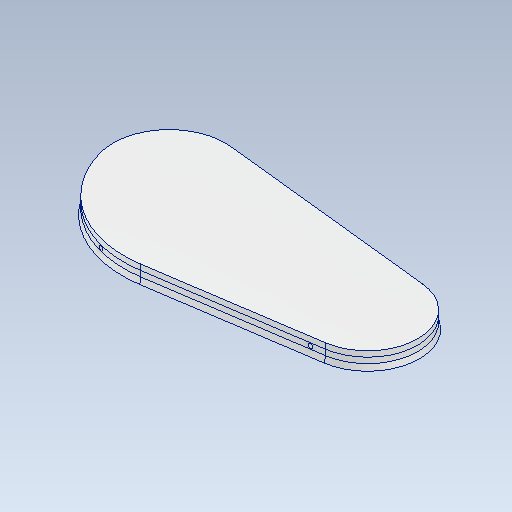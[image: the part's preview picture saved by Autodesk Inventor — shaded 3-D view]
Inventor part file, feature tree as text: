
AUTODESK INVENTOR PART (.ipt)
format: ipt  version: 2021 (Build 250183000, 183)  size: 248,320 bytes
history: native  units: mm
features: sketch x9, extrude x5
ambient origin geometry x8: Origin, YZ Plane, XZ Plane, XY Plane, X Axis, Y Axis, Z Axis, Center Point
bodies: Solid1 (feature_tree), Solid2 (feature_tree), Solid3 (feature_tree)
feature tree (14):
  sketch  "Sketch1"  dims[d0=45.0mm d1=151.164802mm d2=5.0mm d3=0.0mm]
  extrude  "Extrusion1"  Depth=5.0mm TaperAngle=0.0deg
  sketch  "Sketch2"  dims[d4=5.0mm d5=15.0deg d6=45.0mm d7=151.164802mm]
  extrude  "Extrusion2"  Depth=45.0mm
  sketch  "Sketch3"  dims[d9=5.0mm d10=0.0mm d11=40.0mm]
  sketch  "Sketch4"  dims[d12=194.08512mm d13=16.0mm]
  sketch  "Sketch5"  dims[d14=16.0mm d15=16.0mm]
  sketch  "Sketch6"  dims[d16=16.0mm]
  extrude  "Extrusion3"  Depth=5.0mm
  extrude  "Extrusion4"  Depth=16.0mm
  extrude  "Extrusion5"  Depth=16.0mm
  sketch  "Sketch7"  dims[d17=16.0mm]
  sketch  "Sketch8"  dims[d18=16.0mm]
  sketch  "Sketch9"  dims[d19=16.0mm d20=14.0mm d21=14.0mm d22=14.0mm d23=14.0mm d24=14.0mm d25=14.0mm d26=14.0mm d27=14.0mm d28=14.0mm d29=14.0mm d30=14.0mm d31=65.774471mm d32=63.618944mm d33=73.266682mm d34=58.627506mm d35=68.418403mm d36=71.874013mm d37=54.787939mm d38=71.874013mm d39=66.498619mm d40=59.247207mm d41=65.774471mm d42=64.430623mm d43=69.42206mm d44=73.453605mm d45=73.453605mm d46=71.917779mm d47=69.42206mm d48=3.0mm d49=0.0mm d50=4.0mm d51=4.0mm d52=200.0mm d53=0.0mm d54=0.5mm d55=0.872665mm d56=0.5mm d57=0.872665mm]
